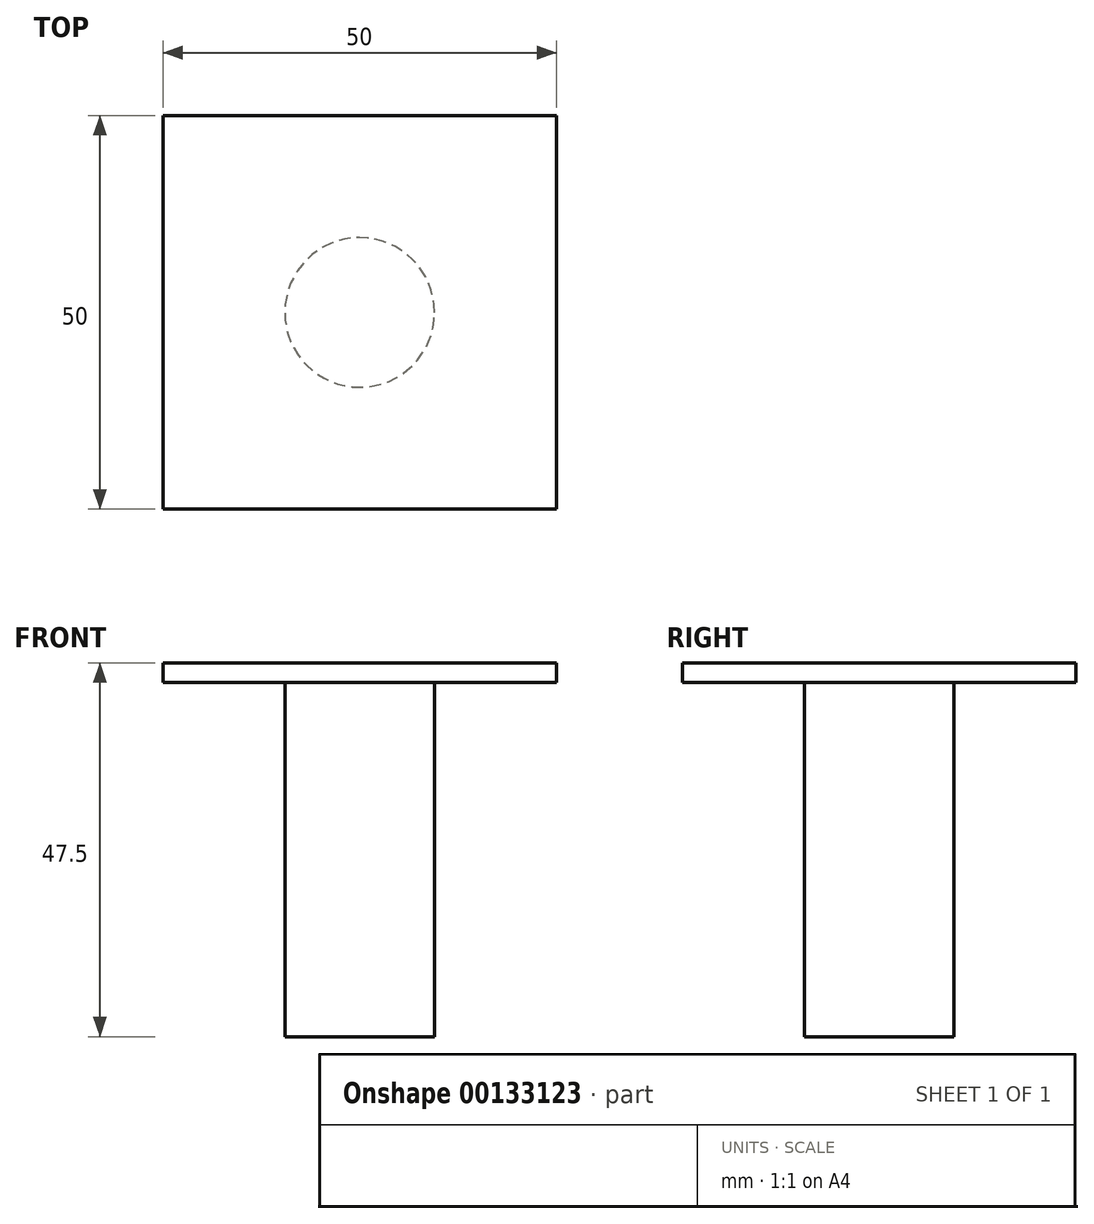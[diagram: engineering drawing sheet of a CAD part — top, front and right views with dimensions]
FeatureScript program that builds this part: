
annotation { "Feature Type Name" : "Feature", "Feature Type Description" : "" }
export const myFeature = defineFeature(function(context is Context, id is Id, definition is map)
    precondition{}
    {
        {
            var Q0;
            Q0=qCreatedBy(makeId("Top.planeOp"),FACE);
            var sketch = newSketch(context, id + "F0", { "sketchPlane" : qUnion([Q0])});
            skLineSegment(sketch, "E0.bottom", {"start": v(0, 6.01) * mm, "end": v(50, 6.01) * mm});
            skLineSegment(sketch, "E0.top", {"start": v(0, 56.01) * mm, "end": v(50, 56.01) * mm});
            skLineSegment(sketch, "E0.left", {"start": v(0, 6.01) * mm, "end": v(0, 56.01) * mm});
            skLineSegment(sketch, "E0.right", {"start": v(50, 6.01) * mm, "end": v(50, 56.01) * mm});
            skLineSegment(sketch, "E1", {"start": v(0, 56.01) * mm, "end": v(50, 6.01) * mm, "construction": true});
            skCircle(sketch, "E2", {"center": v(25, 31.01) * mm, "radius": 9.5 * mm});
            skSolve(sketch);
        }
        {
            var Q0;
            Q0=makeQuery(id+"F0.imprint","IMPRINT",FACE,{"disambiguationData":[TD([[makeQuery(id+"F0.imprint","IMPRINT",EDGE,{"derivedFrom":sQuery(id+"F0.wireOp",EDGE,"E0.bottom")}),1.0]])]});
            var Q1;
            Q1=makeQuery(id+"F0.imprint","IMPRINT",FACE,{"disambiguationData":[TD([[makeQuery(id+"F0.imprint","IMPRINT",EDGE,{"derivedFrom":sQuery(id+"F0.wireOp",EDGE,"E2")}),1.0]])]});
            extrude(context, id + "F1", {"entities" : qUnion([Q0, Q1]), "depth" : 2.5 * mm});
        }
        {
            var Q0;
            Q0=makeQuery(id+"F0.imprint","IMPRINT",FACE,{"disambiguationData":[TD([[makeQuery(id+"F0.imprint","IMPRINT",EDGE,{"derivedFrom":sQuery(id+"F0.wireOp",EDGE,"E2")}),1.0]])]});
            extrude(context, id + "F2", {"entities" : qUnion([Q0]), "operationType" : NewBodyOperationType.ADD, "oppositeDirection" : true, "depth" : 45 * mm});
        }
    });
